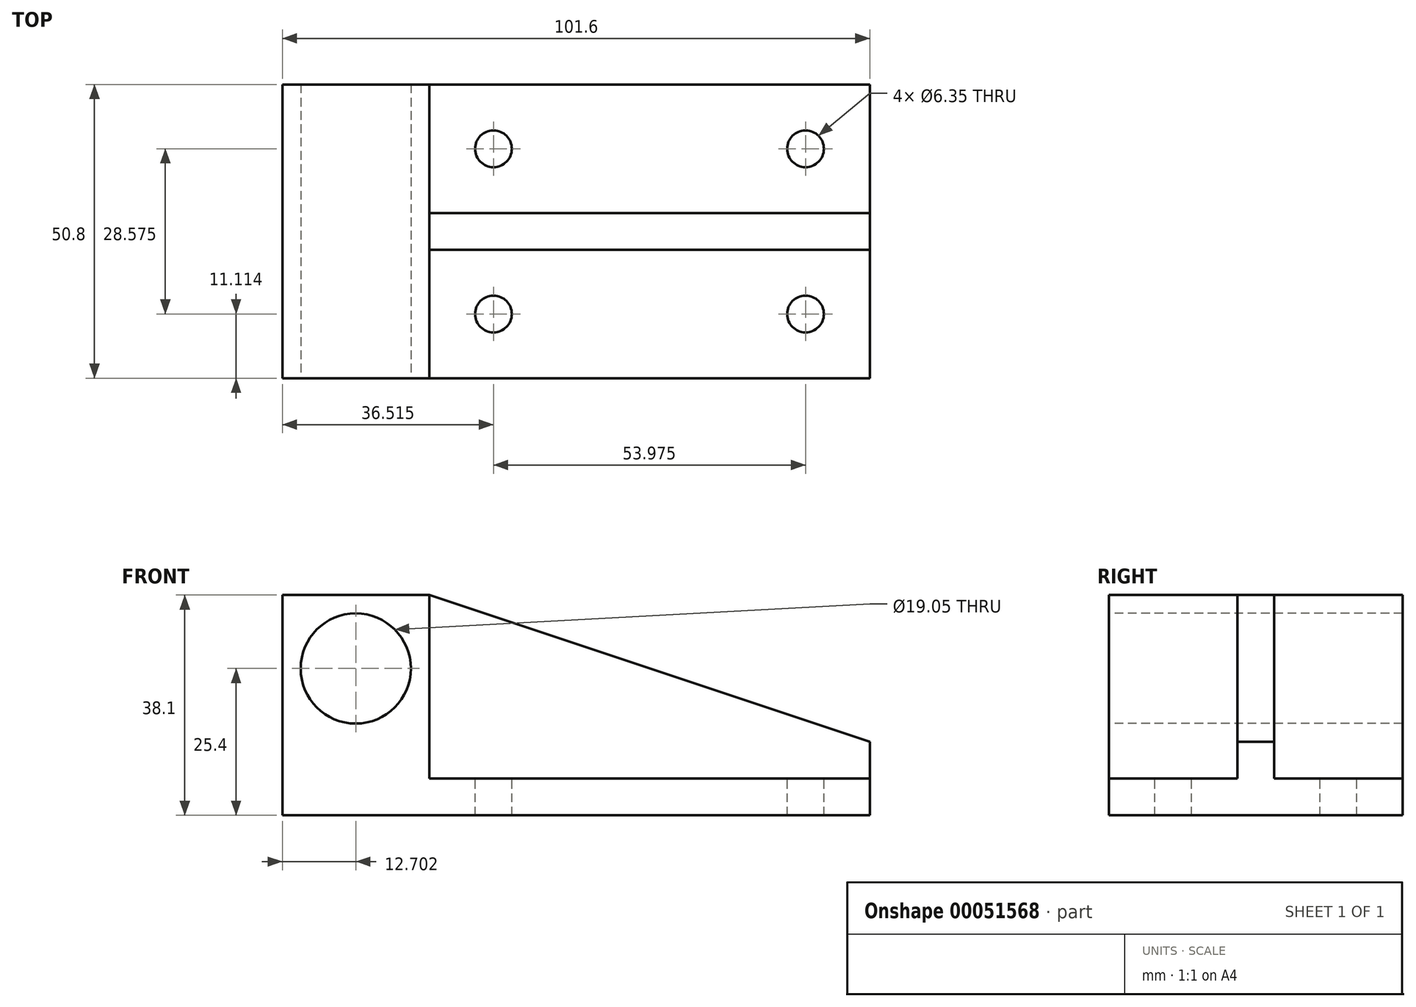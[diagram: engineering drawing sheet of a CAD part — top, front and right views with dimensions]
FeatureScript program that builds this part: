
annotation { "Feature Type Name" : "Feature", "Feature Type Description" : "" }
export const myFeature = defineFeature(function(context is Context, id is Id, definition is map)
    precondition{}
    {
        {
            var Q0;
            Q0=qCreatedBy(makeId("Top.planeOp"),FACE);
            var sketch = newSketch(context, id + "F0", { "sketchPlane" : qUnion([Q0])});
            skLineSegment(sketch, "E0.bottom", {"start": v(-65.43, 16.8) * mm, "end": v(36.17, 16.8) * mm});
            skLineSegment(sketch, "E0.top", {"start": v(-65.43, -34) * mm, "end": v(36.17, -34) * mm});
            skLineSegment(sketch, "E0.left", {"start": v(-65.43, 16.8) * mm, "end": v(-65.43, -34) * mm});
            skLineSegment(sketch, "E0.right", {"start": v(36.17, 16.8) * mm, "end": v(36.17, -34) * mm});
            skSolve(sketch);
        }
        {
            var Q0;
            Q0 = qSketchRegion(id + "F0", true);
            extrude(context, id + "F1", {"entities" : qUnion([Q0]), "depth" : 6.35 * mm});
        }
        {
            var Q0;
            Q0=makeQuery(id+"F1.opExtrude","CAP_FACE",FACE,{"disambiguationData":[OSD([sQuery(id+"F0.wireOp",EDGE,"E0.bottom"),sQuery(id+"F0.wireOp",EDGE,"E0.top"),sQuery(id+"F0.wireOp",EDGE,"E0.left"),sQuery(id+"F0.wireOp",EDGE,"E0.right")])],"isStart":false});
            var sketch = newSketch(context, id + "F2", { "sketchPlane" : qUnion([Q0])});
            skLineSegment(sketch, "E1.bottom", {"start": v(-65.43, 16.8) * mm, "end": v(-40.03, 16.8) * mm});
            skLineSegment(sketch, "E1.top", {"start": v(-65.43, -34) * mm, "end": v(-40.03, -34) * mm});
            skLineSegment(sketch, "E1.left", {"start": v(-65.43, 16.8) * mm, "end": v(-65.43, -34) * mm});
            skLineSegment(sketch, "E1.right", {"start": v(-40.03, 16.8) * mm, "end": v(-40.03, -34) * mm});
            skSolve(sketch);
        }
        {
            var Q0;
            Q0 = qSketchRegion(id + "F2", true);
            extrude(context, id + "F3", {"entities" : qUnion([Q0]), "operationType" : NewBodyOperationType.ADD, "depth" : 31.75 * mm});
        }
        {
            var Q0;
            Q0=makeQuery(id+"F3.boolean.opBoolean","MERGE",FACE,{"derivedFrom":[makeQuery(id+"F1.opExtrude","SWEPT_FACE",FACE,{"disambiguationData":[OSD([sQuery(id+"F0.wireOp",EDGE,"E0.top")])]}),makeQuery(id+"F3.opExtrude","SWEPT_FACE",FACE,{"disambiguationData":[OSD([sQuery(id+"F2.wireOp",EDGE,"E1.top")])]})]});
            var sketch = newSketch(context, id + "F4", { "sketchPlane" : qUnion([Q0])});
            skCircle(sketch, "E2", {"center": v(-52.73, 25.4) * mm, "radius": 9.53 * mm});
            skSolve(sketch);
        }
        {
            var Q0;
            Q0 = qSketchRegion(id + "F4", true);
            extrude(context, id + "F5", {"entities" : qUnion([Q0]), "operationType" : NewBodyOperationType.REMOVE, "endBound" : BoundingType.THROUGH_ALL, "oppositeDirection" : true, "depth" : 25.4 * mm});
        }
        {
            var Q0;
            Q0=makeQuery(id+"F1.opExtrude","CAP_FACE",FACE,{"disambiguationData":[OSD([sQuery(id+"F0.wireOp",EDGE,"E0.bottom"),sQuery(id+"F0.wireOp",EDGE,"E0.top"),sQuery(id+"F0.wireOp",EDGE,"E0.left"),sQuery(id+"F0.wireOp",EDGE,"E0.right")])],"isStart":false});
            var sketch = newSketch(context, id + "F6", { "sketchPlane" : qUnion([Q0])});
            skLineSegment(sketch, "E3.bottom", {"start": v(36.17, -5.42) * mm, "end": v(-40.03, -5.42) * mm});
            skLineSegment(sketch, "E3.top", {"start": v(36.17, -11.77) * mm, "end": v(-40.03, -11.77) * mm});
            skLineSegment(sketch, "E3.left", {"start": v(36.17, -5.42) * mm, "end": v(36.17, -11.77) * mm});
            skLineSegment(sketch, "E3.right", {"start": v(-40.03, -5.42) * mm, "end": v(-40.03, -11.77) * mm});
            skSolve(sketch);
        }
        {
            var Q0;
            Q0 = qSketchRegion(id + "F6", true);
            extrude(context, id + "F7", {"entities" : qUnion([Q0]), "operationType" : NewBodyOperationType.ADD, "depth" : 6.35 * mm});
        }
        {
            var Q0;
            Q0=makeQuery(id+"F7.opExtrude","CAP_FACE",FACE,{"disambiguationData":[OSD([sQuery(id+"F6.wireOp",EDGE,"E3.bottom"),sQuery(id+"F6.wireOp",EDGE,"E3.top"),sQuery(id+"F6.wireOp",EDGE,"E3.left"),sQuery(id+"F6.wireOp",EDGE,"E3.right")])],"isStart":false});
            extrude(context, id + "F8", {"entities" : qUnion([Q0]), "operationType" : NewBodyOperationType.ADD, "depth" : 25.4 * mm});
        }
        {
            var Q0;
            Q0=makeQuery(id+"F8.opExtrude","CAP_EDGE",EDGE,{"disambiguationData":[OSD([sQuery(id+"F6.wireOp",EDGE,"E3.left")])],"isStart":false});
            chamfer(context, id + "F9", {"entities" : qUnion([Q0]), "chamferType" : ChamferType.OFFSET_ANGLE, "width" : 76.2 * mm, "oppositeDirection" : true, "angle" : 18.4 * degree, "tangentPropagation" : true});
        }
        {
            var Q0;
            {var subQ0=sQuery(id+"F0.wireOp",EDGE,"E0.right");var subQ1=sQuery(id+"F0.wireOp",EDGE,"E0.bottom");Q0=makeQuery(id+"F7.boolean.opBoolean","SPLIT",FACE,{"disambiguationData":[TD([makeQuery(id+"F1.opExtrude","SWEPT_FACE",FACE,{"disambiguationData":[OSD([subQ1])]})])],"derivedFrom":makeQuery(id+"F1.opExtrude","CAP_FACE",FACE,{"disambiguationData":[OSD([subQ1,sQuery(id+"F0.wireOp",EDGE,"E0.top"),sQuery(id+"F0.wireOp",EDGE,"E0.left"),subQ0])],"isStart":false})});}
            var sketch = newSketch(context, id + "F10", { "sketchPlane" : qUnion([Q0])});
            skCircle(sketch, "E4", {"center": v(25.06, 5.69) * mm, "radius": 3.18 * mm});
            skCircle(sketch, "E5", {"center": v(-28.92, 5.69) * mm, "radius": 3.18 * mm});
            skSolve(sketch);
        }
        {
            var Q0;
            Q0 = qSketchRegion(id + "F10", true);
            extrude(context, id + "F11", {"entities" : qUnion([Q0]), "operationType" : NewBodyOperationType.REMOVE, "oppositeDirection" : true, "depth" : 25.4 * mm});
        }
        {
            var Q0;
            {var subQ0=sQuery(id+"F0.wireOp",EDGE,"E0.right");var subQ1=sQuery(id+"F0.wireOp",EDGE,"E0.top");Q0=makeQuery(id+"F7.boolean.opBoolean","SPLIT",FACE,{"disambiguationData":[TD([makeQuery(id+"F1.opExtrude","SWEPT_FACE",FACE,{"disambiguationData":[OSD([subQ1])]})])],"derivedFrom":makeQuery(id+"F1.opExtrude","CAP_FACE",FACE,{"disambiguationData":[OSD([sQuery(id+"F0.wireOp",EDGE,"E0.bottom"),subQ1,sQuery(id+"F0.wireOp",EDGE,"E0.left"),subQ0])],"isStart":false})});}
            var sketch = newSketch(context, id + "F12", { "sketchPlane" : qUnion([Q0])});
            skCircle(sketch, "E6", {"center": v(-28.92, -22.89) * mm, "radius": 3.18 * mm});
            skCircle(sketch, "E7", {"center": v(25.06, -22.89) * mm, "radius": 3.18 * mm});
            skSolve(sketch);
        }
        {
            var Q0;
            Q0 = qSketchRegion(id + "F12", true);
            extrude(context, id + "F13", {"entities" : qUnion([Q0]), "operationType" : NewBodyOperationType.REMOVE, "oppositeDirection" : true, "depth" : 25.4 * mm});
        }
    });
